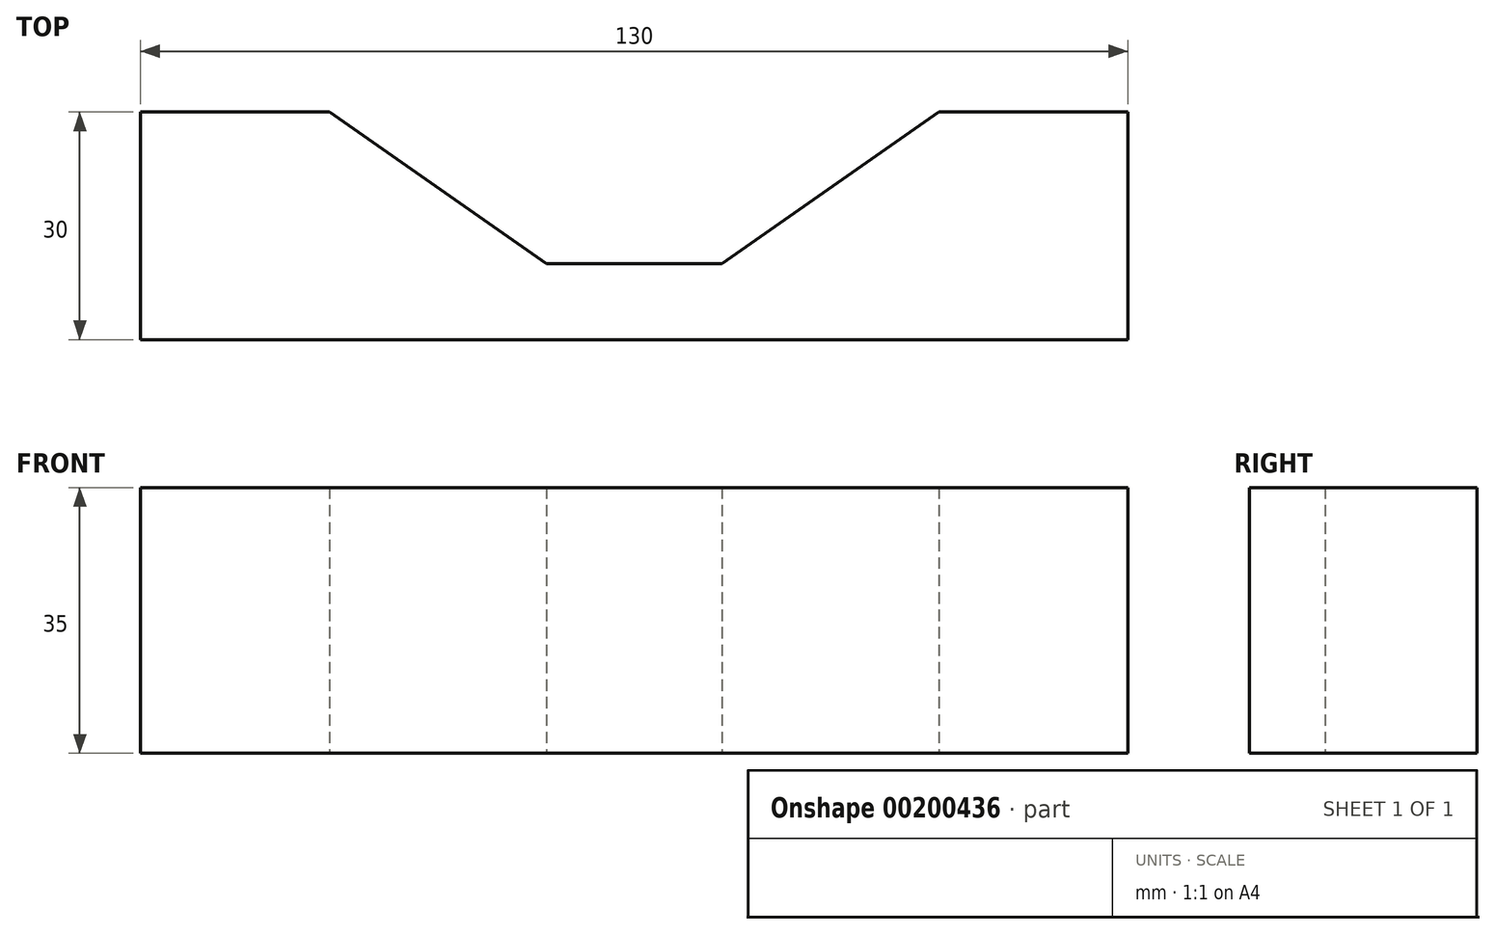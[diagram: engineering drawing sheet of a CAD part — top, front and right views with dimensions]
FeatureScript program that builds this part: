
annotation { "Feature Type Name" : "Feature", "Feature Type Description" : "" }
export const myFeature = defineFeature(function(context is Context, id is Id, definition is map)
    precondition{}
    {
        {
            var Q0;
            Q0=qCreatedBy(makeId("Top.planeOp"),FACE);
            var sketch = newSketch(context, id + "F0", { "sketchPlane" : qUnion([Q0])});
            skCircle(sketch, "E0.cCircle", {"center": v(0, 0) * mm, "radius": 55 * mm, "construction": true});
            skPoint(sketch, "E0.0.midPoint", {"position": v(0, 55) * mm});
            skLineSegment(sketch, "E1", {"start": v(-65, -69.05) * mm, "end": v(65, -69.05) * mm});
            skLineSegment(sketch, "E2", {"start": v(65, -69.05) * mm, "end": v(65, -39.05) * mm});
            skLineSegment(sketch, "E3", {"start": v(65, -39.05) * mm, "end": v(40.13, -39.05) * mm});
            skLineSegment(sketch, "E4", {"start": v(-65, -39.05) * mm, "end": v(-65, -69.05) * mm});
            skLineSegment(sketch, "E5", {"start": v(-40.13, -39.05) * mm, "end": v(-11.56, -59.05) * mm});
            skLineSegment(sketch, "E6", {"start": v(-11.56, -59.05) * mm, "end": v(0, -59.05) * mm});
            skPoint(sketch, "E7", {"position": v(0, -69.05) * mm});
            skPoint(sketch, "E8.orphan", {"position": v(-11.56, -59.05) * mm});
            skLineSegment(sketch, "E9", {"start": v(0, 0) * mm, "end": v(0, -83.1) * mm, "construction": true});
            skLineSegment(sketch, "E10.MirrorCS", {"start": v(40.13, -39.05) * mm, "end": v(11.56, -59.05) * mm});
            skLineSegment(sketch, "E11.MirrorCS", {"start": v(11.56, -59.05) * mm, "end": v(0, -59.05) * mm});
            skLineSegment(sketch, "E12.trimOffspring", {"start": v(-40.13, -39.05) * mm, "end": v(-65, -39.05) * mm});
            skSolve(sketch);
        }
        {
            var Q0;
            Q0 = qSketchRegion(id + "F0", true);
            extrude(context, id + "F1", {"entities" : qUnion([Q0]), "depth" : 35 * mm});
        }
    });
